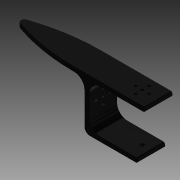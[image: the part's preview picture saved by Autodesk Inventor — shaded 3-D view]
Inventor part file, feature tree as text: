
AUTODESK INVENTOR PART (.ipt)
format: ipt  version: 2014 SP2 (Build 180246200, 246)  size: 339,456 bytes
history: native  units: in
note: dims shown in document units (in); Inventor stores cm internally (conversion verified against a paired STEP export)
features: sketch x16, extrude x15, fillet x6, projected_geometry x5, mirror x4, pattern_circular x3, plane x2
ambient origin geometry x8: Origin, YZ Plane, XZ Plane, XY Plane, X Axis, Y Axis, Z Axis, Center Point
bodies: Solid1 (feature_tree)
feature tree (51):
  extrude  "Extrusion1"  Depth=0.1181in
  mirror  "Mirror1"
  mirror  "Mirror2"
  extrude  "Extrusion4"  Depth=0.1181in
  mirror  "Mirror3"
  extrude  "Extrusion11"  Depth=0.1969in TaperAngle=0.0deg
  extrude  "Extrusion13"  Depth=0.0787in
  mirror  "Mirror4"
  extrude  "Extrusion14"  Depth=0.3937in
  pattern_circular  "Circular Pattern6"  Count=4 Angle=360.0deg
  extrude  "Extrusion15"  Depth=0.6299in
  pattern_circular  "Circular Pattern7"  Count=4 Angle=360.0deg
  extrude  "Extrusion16"  Depth=0.0787in
  plane  "Work Plane1"
  extrude  "Extrusion17"  Depth=0.1575in
  plane  "Work Plane3"
  extrude  "Extrusion18"  Depth=0.1181in
  sketch  "Sketch24"  dims[d78=0.5118in d79=0.6299in]
  extrude  "Extrusion22"  Depth=0.0787in
  sketch  "Sketch25"  dims[d80=0.1181in]
  extrude  "Extrusion23"  Depth=0.0591in
  extrude  "Extrusion24"  Depth=0.3937in
  pattern_circular  "Circular Pattern8"  [2 undecoded]
  extrude  "Extrusion25"  Depth=0.3937in TaperAngle=0.0deg
  extrude  "Extrusion26"  Depth=0.1181in
  extrude  "Extrusion27"  Depth=0.0787in TaperAngle=0.0deg
  fillet  "Fillet9"  Radius=0.1181in
  fillet  "Fillet10"  Radius=0.5118in
  fillet  "Fillet11"  Radius=0.1181in
  fillet  "Fillet12"  Radius=0.6299in
  fillet  "Fillet13"  Radius=0.3937in
  fillet  "Fillet14"  Radius=1.5748in
  sketch  "Sketch1"  dims[d0=0.7087in d1=0.1181in]
  sketch  "Sketch4"  dims[d2=0.1181in d3=2.2047in]
  projected_geometry  "Projected Loop1"
  sketch  "Sketch11"  dims[d4=0.3937in d5=0.0in d16=0.1969in d17=0.0in]
  projected_geometry  "Projected Loop3"
  sketch  "Sketch13"  dims[d54=0.3937in d55=0.0in d65=0.0787in]
  sketch  "Sketch14"  dims[d66=0.3937in d67=0.0in d68=0.5118in]
  sketch  "Sketch15"  dims[d69=0.8661in]
  sketch  "Sketch16"  dims[d71=0.1181in]
  projected_geometry  "Projected Loop4"
  sketch  "Sketch17"  dims[d72=0.1181in]
  sketch  "Sketch18"  dims[d73=0.3937in d74=0.0in d75=1.5748in d76=360.0deg]
  projected_geometry  "Projected Loop5"
  sketch  "Sketch26"  dims[d81=0.1181in]
  projected_geometry  "Projected Loop6"
  sketch  "Sketch27"  dims[d82=0.3937in d83=0.0in d84=1.5748in d85=360.0deg]
  sketch  "Sketch28"  dims[d90=0.5512in d91=0.0in d92=0.0787in]
  sketch  "Sketch29"  dims[d93=1.5748in d94=0.0in d95=0.1575in]
  sketch  "Sketch30"  dims[d96=1.378in d97=0.0in d110=0.1181in d111=0.0787in d112=0.0591in d113=0.0984in d114=1.0236in d115=3.0807in d116=0.0in d117=0.1181in d118=0.0787in d119=0.0in d120=0.1181in d121=0.5118in d122=0.1181in d123=0.6299in d124=0.3937in d125=0.0in d126=1.5748in d127=360.0deg d129=0.1575in d130=0.3937in d131=0.0in d132=3.1201in d133=0.0in d134=3.1201in d135=0.0in d136=0.1181in d137=0.3937in d138=0.3937in d139=0.1969in d140=0.0787in d141=0.3937in]
note: 2 required parameter values undecoded (feature->parameter linkage not recoverable at this tier; creation-order binding heuristic only, values carry confidence <= 0.55)
